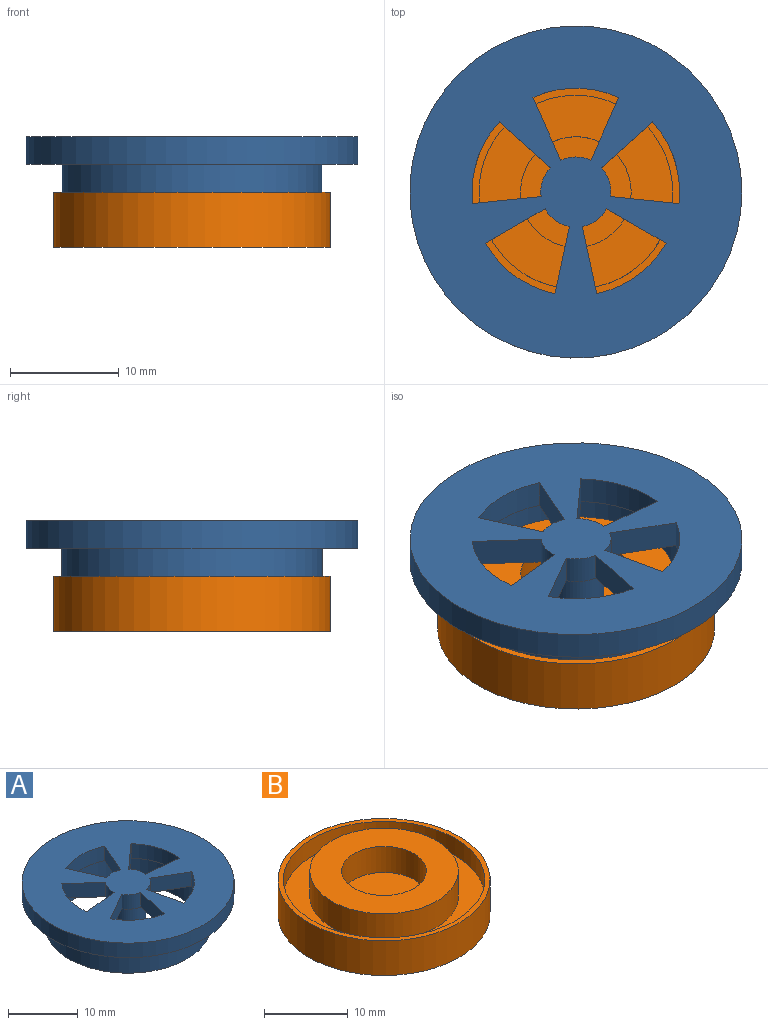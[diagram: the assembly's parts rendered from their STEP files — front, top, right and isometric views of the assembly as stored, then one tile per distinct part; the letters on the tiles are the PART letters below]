
ASSEMBLY  parts=2 mates=1
PART A: 29 faces, bbox 30.5x30.5x7.6 mm
  f0: cylinder r=15.24mm len=30.48mm, axis (0,0,-1), area 243.2mm2, adj f1,f2
  f1: plane 30.48x30.48mm, normal (0,0,1), area 556.5mm2, adj f0,f9,f10,f11,f12,f13,f14,f15
  f2: plane 30.48x30.48mm, normal (0,0,-1), area 281.9mm2, adj f0,f4
  f3: cylinder r=10.16mm len=20.32mm, axis (0,0,-1), area 324.3mm2, adj f5,f6
  f4: cylinder r=11.94mm len=23.88mm, axis (0,0,-1), area 381mm2, adj f2,f5
  f5: plane 23.88x23.88mm, normal (0,0,-1), area 123.4mm2, adj f3,f4
  f6: plane 20.32x20.32mm, normal (0,0,-1), area 130.9mm2, adj f3,f7,f9,f10,f11,f12,f13,f14
  f7: cylinder r=2.54mm len=5.08mm, axis (0,0,-1), area 81.1mm2, adj f6,f8
  f8: plane 5.08x5.08mm, normal (0,0,-1), area 20.3mm2, adj f7
  f9: plane 4.7x4.21mm, normal (0.67,-0.74,0), area 16mm2, adj f1,f6,f10,f12
  f10: cylinder r=9.53mm len=7.49mm, axis (0,0,-1), area 20.6mm2, adj f1,f6,f9,f11
  f11: plane 6.28x2.54mm, normal (0.1,0.99,0), area 16mm2, adj f1,f6,f10,f12
  f12: cylinder r=3.21mm len=2.63mm, axis (0,0,-1), area 7.3mm2, adj f1,f6,f9,f11
  f13: plane 5.46x3.17mm, normal (-0.5,-0.86,0), area 16mm2, adj f1,f6,f14,f16
  f14: cylinder r=9.53mm len=6.37mm, axis (0,0,-1), area 20.6mm2, adj f1,f6,f13,f15
  f15: plane 6.17x2.54mm, normal (0.98,0.21,0), area 16mm2, adj f1,f6,f14,f16
  f16: cylinder r=3.21mm len=2.54mm, axis (0,0,-1), area 7.3mm2, adj f1,f6,f13,f15
  f17: plane 6.17x2.54mm, normal (-0.98,0.21,0), area 16mm2, adj f1,f6,f18,f20
  f18: cylinder r=9.53mm len=6.37mm, axis (0,0,-1), area 20.6mm2, adj f1,f6,f17,f19
  f19: plane 5.46x3.17mm, normal (0.5,-0.86,0), area 16mm2, adj f1,f6,f18,f20
  f20: cylinder r=3.21mm len=2.54mm, axis (0,0,-1), area 7.3mm2, adj f1,f6,f17,f19
  f21: cylinder r=9.53mm len=7.87mm, axis (0,0,-1), area 20.6mm2, adj f1,f6,f22,f24
  f22: plane 5.77x2.55mm, normal (-0.91,0.4,0), area 16mm2, adj f1,f6,f21,f23
  f23: cylinder r=3.21mm len=2.77mm, axis (0,0,-1), area 7.3mm2, adj f1,f6,f22,f24
  f24: plane 5.77x2.55mm, normal (0.91,0.4,0), area 16mm2, adj f1,f6,f21,f23
  f25: plane 6.28x2.54mm, normal (-0.1,0.99,0), area 16mm2, adj f1,f6,f26,f28
  f26: cylinder r=9.53mm len=7.49mm, axis (0,0,-1), area 20.6mm2, adj f1,f6,f25,f27
  f27: plane 4.7x4.21mm, normal (-0.67,-0.74,0), area 16mm2, adj f1,f6,f26,f28
  f28: cylinder r=3.21mm len=2.63mm, axis (0,0,-1), area 7.3mm2, adj f1,f6,f25,f27
PART B: 9 faces, bbox 25.4x25.4x6.4 mm
  f0: plane 24.13x24.13mm, normal (0,0,1), area 209mm2, adj f2,f5
  f1: cylinder r=5.08mm len=10.16mm, axis (0,0,-1), area 121.6mm2, adj f3,f4
  f2: cylinder r=8.89mm len=17.78mm, axis (0,0,-1), area 212.8mm2, adj f0,f3
  f3: plane 17.78x17.78mm, normal (0,0,1), area 167.2mm2, adj f1,f2
  f4: plane 10.16x10.16mm, normal (0,0,1), area 81.1mm2, adj f1
  f5: cylinder r=12.06mm len=24.13mm, axis (0,0,-1), area 192.5mm2, adj f0,f6
  f6: plane 25.4x25.4mm, normal (0,0,1), area 49.4mm2, adj f5,f8
  f7: plane 25.4x25.4mm, normal (0,0,-1), area 506.7mm2, adj f8
  f8: cylinder r=12.7mm len=25.4mm, axis (0,0,-1), area 405.4mm2, adj f6,f7
PLACE A t=(-35.27,18.79,-0.63)mm
PLACE B t=(15.53,18.79,-3.17)mm
MATE fastened A.f0 <-> B.f1  axis (0,0,-1) through (15.53,18.79,-0.63)mm
